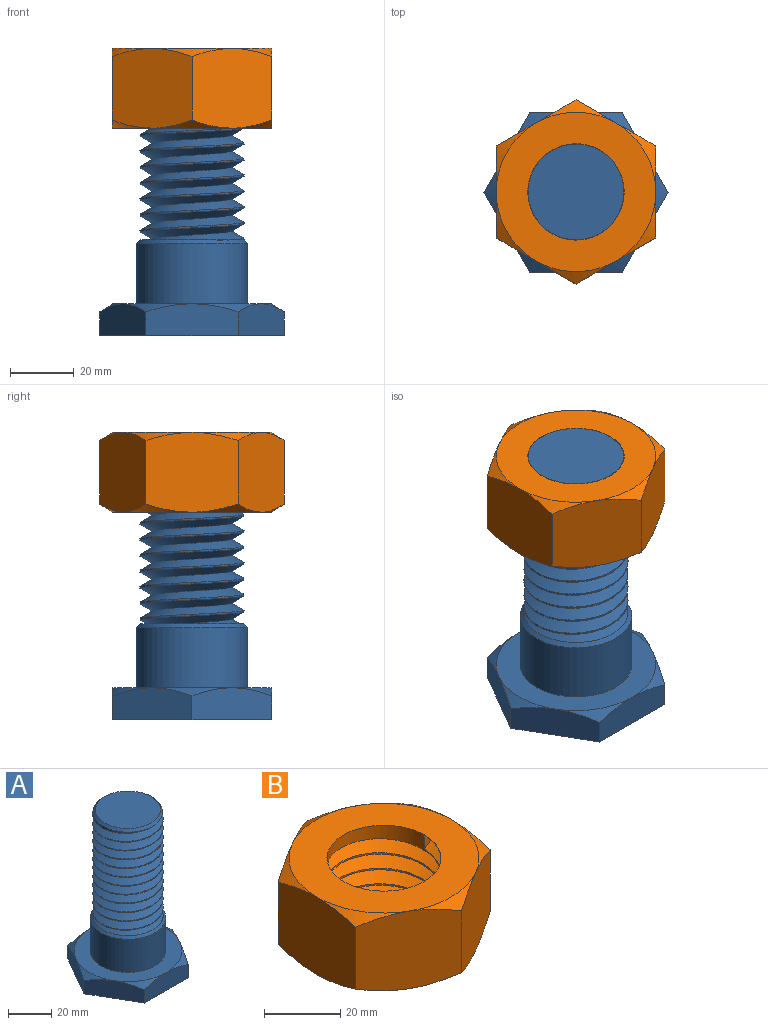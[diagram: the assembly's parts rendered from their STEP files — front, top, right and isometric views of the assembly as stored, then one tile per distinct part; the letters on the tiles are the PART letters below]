
ASSEMBLY  parts=2 mates=1
PART A: 24 faces, bbox 57.7x57.7x90 mm
  f0: plane 50x50mm, normal (0,0,1), area 1001.4mm2, adj f2,f11,f12,f13,f14,f15,f16
  f1: cylinder r=16.3mm len=58.8mm, axis (0,0,-1), area 755.8mm2, adj f3,f6,f7,f9,f10
  f2: cylinder r=17.5mm len=35mm, axis (0,0,-1), area 2067.2mm2, adj f0,f3
  f3: cone r=16.3mm half-angle=45deg, axis (0,0,-1), area 180.2mm2, adj f1,f2,f8
  f4: plane 30.2x30.2mm, normal (0,0,1), area 716.3mm2, adj f10
  f5: plane 4.5x3.9mm, normal (0,1,0), area 8.8mm2, adj f7,f8,f9
  f6: plane 4.06x3.9mm, normal (0,-1,0), area 8.3mm2, adj f1,f7,f9,f10
  f7: bspline ~62.25x37.64mm, area 4863.9mm2, adj f1,f5,f6,f9,f10
  f8: cylinder r=16.3mm len=32.6mm, axis (0,0,1), area 207.6mm2, adj f3,f5,f9
  f9: bspline ~62.25x37.64mm, area 4886.4mm2, adj f1,f5,f6,f7,f8
  f10: cone r=15.1mm half-angle=45deg, axis (0,0,-1), area 154.4mm2, adj f1,f4,f6,f7
  f11: cone r=32.25mm half-angle=57deg, axis (0,0,-1), area 40mm2, adj f0,f18,f19
  f12: cone r=32.25mm half-angle=57deg, axis (0,0,-1), area 40mm2, adj f0,f18,f23
  f13: cone r=32.25mm half-angle=57deg, axis (0,0,-1), area 40mm2, adj f0,f19,f20
  f14: cone r=32.25mm half-angle=57deg, axis (0,0,-1), area 40mm2, adj f0,f20,f21
  f15: cone r=32.25mm half-angle=57deg, axis (0,0,-1), area 40mm2, adj f0,f21,f22
  f16: cone r=32.25mm half-angle=57deg, axis (0,0,-1), area 40mm2, adj f0,f22,f23
  f17: plane 57.74x50mm, normal (0,0,-1), area 2165.1mm2, adj f18,f19,f20,f21,f22,f23
  f18: plane 28.89x10mm, normal (0,-1,0), area 263.8mm2, adj f11,f12,f17,f19,f23
  f19: plane 25x14.43mm, normal (-0.87,-0.5,0), area 263.8mm2, adj f11,f13,f17,f18,f20
  f20: plane 25x14.43mm, normal (-0.87,0.5,0), area 263.8mm2, adj f13,f14,f17,f19,f21
  f21: plane 28.89x10mm, normal (0,1,0), area 263.8mm2, adj f14,f15,f17,f20,f22
  f22: plane 25x14.43mm, normal (0.87,0.5,0), area 263.8mm2, adj f15,f16,f17,f21,f23
  f23: plane 25x14.43mm, normal (0.87,-0.5,0), area 263.8mm2, adj f12,f16,f17,f18,f22
PART B: 24 faces, bbox 57.7x57.7x27.8 mm
  f0: plane 50x50mm, normal (0,0,1), area 1256.6mm2, adj f2,f8,f9,f11,f13,f15,f17
  f1: plane 50x50mm, normal (0,0,-1), area 1077mm2, adj f2,f3,f4,f6,f7,f10,f12,f14
  f2: cylinder r=15mm len=30mm, axis (0,0,1), area 440mm2, adj f0,f1,f3,f4,f5
  f3: bspline ~43.64x37.79mm, area 2286.2mm2, adj f1,f2,f4,f5
  f4: bspline ~43.64x37.79mm, area 2080.4mm2, adj f1,f2,f3,f5
  f5: plane 4.5x3.9mm, normal (0,-1,0), area 8.8mm2, adj f2,f3,f4
  f6: cone r=39.5mm half-angle=56.8deg, axis (0,0,1), area 40.2mm2, adj f1,f18,f19
  f7: cone r=39.5mm half-angle=56.8deg, axis (0,0,1), area 40.2mm2, adj f1,f18,f23
  f8: cone r=39.5mm half-angle=56.8deg, axis (0,0,-1), area 40.2mm2, adj f0,f18,f19
  f9: cone r=39.5mm half-angle=56.8deg, axis (0,0,-1), area 40.2mm2, adj f0,f18,f23
  f10: cone r=39.5mm half-angle=56.8deg, axis (0,0,1), area 40.2mm2, adj f1,f19,f20
  f11: cone r=39.5mm half-angle=56.8deg, axis (0,0,-1), area 40.2mm2, adj f0,f19,f20
  f12: cone r=39.5mm half-angle=56.8deg, axis (0,0,1), area 40.2mm2, adj f1,f20,f21
  f13: cone r=39.5mm half-angle=56.8deg, axis (0,0,-1), area 40.2mm2, adj f0,f20,f21
  f14: cone r=39.5mm half-angle=56.8deg, axis (0,0,1), area 40.2mm2, adj f1,f21,f22
  f15: cone r=39.5mm half-angle=56.8deg, axis (0,0,-1), area 40.2mm2, adj f0,f21,f22
  f16: cone r=39.5mm half-angle=56.8deg, axis (0,0,1), area 40.2mm2, adj f1,f22,f23
  f17: cone r=39.5mm half-angle=56.8deg, axis (0,0,-1), area 40.2mm2, adj f0,f22,f23
  f18: plane 25.02x25mm, normal (-0.5,-0.87,0), area 671.5mm2, adj f6,f7,f8,f9,f19,f23
  f19: plane 28.89x25.01mm, normal (-1,0,0), area 671.5mm2, adj f6,f8,f10,f11,f18,f20
  f20: plane 25.02x25mm, normal (-0.5,0.87,0), area 671.5mm2, adj f10,f11,f12,f13,f19,f21
  f21: plane 25.02x25mm, normal (0.5,0.87,0), area 671.5mm2, adj f12,f13,f14,f15,f20,f22
  f22: plane 28.89x25.01mm, normal (1,0,0), area 671.5mm2, adj f14,f15,f16,f17,f21,f23
  f23: plane 25.02x25mm, normal (0.5,-0.87,0), area 671.5mm2, adj f7,f9,f16,f17,f18,f22
PLACE A t=(-46.14,2.73,-1.17)mm fixed
PLACE B t=(-46.14,2.73,63.83)mm
MATE cylindrical A.f1 <-> B.f6  axis (0,0,1) through (-46.14,2.73,88.83)mm
